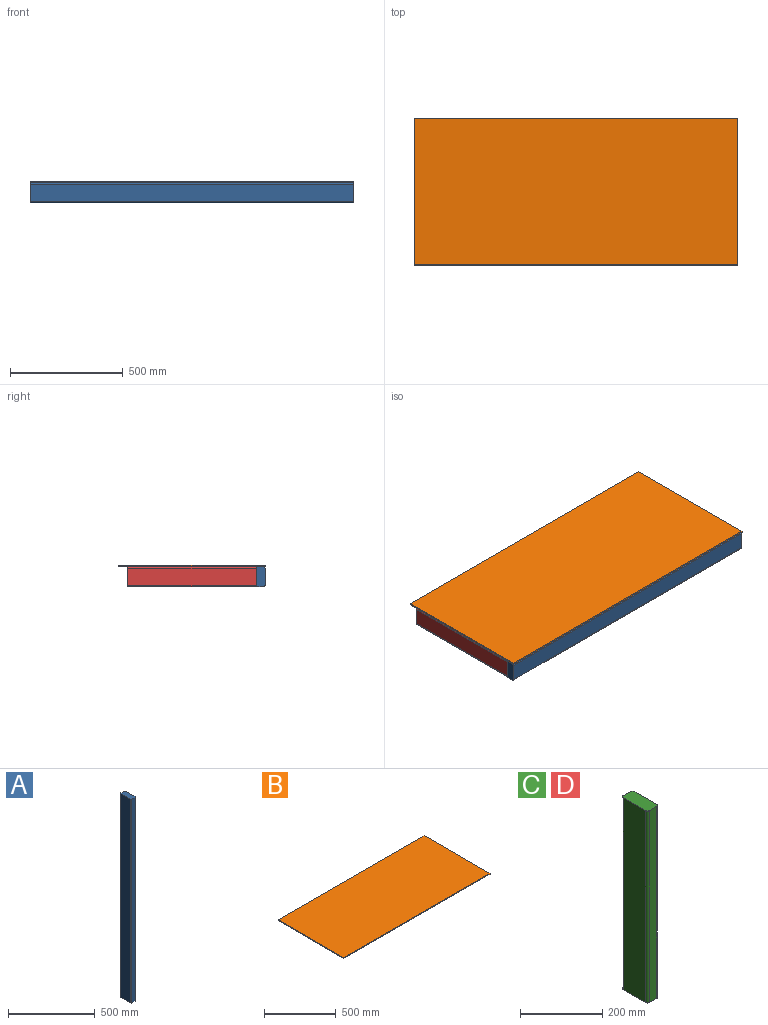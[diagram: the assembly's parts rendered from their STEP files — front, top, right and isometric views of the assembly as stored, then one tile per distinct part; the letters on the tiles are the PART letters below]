
ASSEMBLY  parts=4 mates=9
PART A: 10 faces, bbox 38.1x88.9x1435.1 mm
  f0: plane 1435.1x76.2mm, normal (-1,0,0), area 109354.6mm2, adj f1,f7,f8,f9
  f1: cylinder r=6.35mm len=1435.1mm, axis (0,0,-1), area 14314.5mm2, adj f0,f2,f8,f9
  f2: plane 1435.1x25.4mm, normal (0,-1,0), area 36451.5mm2, adj f1,f3,f8,f9
  f3: cylinder r=6.35mm len=1435.1mm, axis (0,0,-1), area 14314.5mm2, adj f2,f4,f8,f9
  f4: plane 1435.1x76.2mm, normal (1,0,0), area 109354.6mm2, adj f3,f5,f8,f9
  f5: cylinder r=6.35mm len=1435.1mm, axis (0,0,-1), area 14314.5mm2, adj f4,f6,f8,f9
  f6: plane 1435.1x25.4mm, normal (0,1,0), area 36451.5mm2, adj f5,f7,f8,f9
  f7: cylinder r=6.35mm len=1435.1mm, axis (0,0,-1), area 14314.5mm2, adj f0,f6,f8,f9
  f8: plane 88.9x38.1mm, normal (0,0,1), area 3352.5mm2, adj f0,f1,f2,f3,f4,f5,f6,f7
  f9: plane 88.9x38.1mm, normal (0,0,-1), area 3352.5mm2, adj f0,f1,f2,f3,f4,f5,f6,f7
PART B: 6 faces, bbox 1435.1x647.7x6.4 mm
  f0: plane 1435.1x6.35mm, normal (0,1,0), area 9112.9mm2, adj f1,f3,f4,f5
  f1: plane 647.7x6.35mm, normal (-1,0,0), area 4112.9mm2, adj f0,f2,f4,f5
  f2: plane 1435.1x6.35mm, normal (0,-1,0), area 9112.9mm2, adj f1,f3,f4,f5
  f3: plane 647.7x6.35mm, normal (1,0,0), area 4112.9mm2, adj f0,f2,f4,f5
  f4: plane 1435.1x647.7mm, normal (0,0,1), area 929514.3mm2, adj f0,f1,f2,f3
  f5: plane 1435.1x647.7mm, normal (0,0,-1), area 929514.3mm2, adj f0,f1,f2,f3
PART C: 10 faces, bbox 38.1x88.9x571.5 mm
  f0: plane 571.5x76.2mm, normal (-1,0,0), area 43548.3mm2, adj f1,f7,f8,f9
  f1: cylinder r=6.35mm len=571.5mm, axis (0,0,-1), area 5700.5mm2, adj f0,f2,f8,f9
  f2: plane 571.5x25.4mm, normal (0,-1,0), area 14516.1mm2, adj f1,f3,f8,f9
  f3: cylinder r=6.35mm len=571.5mm, axis (0,0,-1), area 5700.5mm2, adj f2,f4,f8,f9
  f4: plane 571.5x76.2mm, normal (1,0,0), area 43548.3mm2, adj f3,f5,f8,f9
  f5: cylinder r=6.35mm len=571.5mm, axis (0,0,-1), area 5700.5mm2, adj f4,f6,f8,f9
  f6: plane 571.5x25.4mm, normal (0,1,0), area 14516.1mm2, adj f5,f7,f8,f9
  f7: cylinder r=6.35mm len=571.5mm, axis (0,0,-1), area 5700.5mm2, adj f0,f6,f8,f9
  f8: plane 88.9x38.1mm, normal (0,0,1), area 3352.5mm2, adj f0,f1,f2,f3,f4,f5,f6,f7
  f9: plane 88.9x38.1mm, normal (0,0,-1), area 3352.5mm2, adj f0,f1,f2,f3,f4,f5,f6,f7
PART D: same geometry as C
PLACE A rot(axis=(-0.58,0.58,-0.58),120deg) t=(717.55,18.66,-50.15)mm
PLACE B t=(717.55,323.85,-6.35)mm
PLACE C rot(axis=(0,0.71,0.71),180deg) t=(1416.18,323.85,-50.67)mm
PLACE D rot(axis=(1,0,0),90deg) t=(18.92,323.85,-50.67)mm
MATE planar A.f4 <-> B.f2  axis (0,-1,0) through (717.55,0,-50.8)mm
MATE planar A.f8 <-> B.f3  axis (1,0,0) through (1435.1,19.05,-50.8)mm
MATE planar A.f2 <-> B.f5  axis (0,0,1) through (717.55,19.05,-6.35)mm
MATE planar B.f5 <-> D.f6  axis (0,0,-1) through (717.55,323.85,-6.35)mm
MATE planar C.f0 <-> B.f3  axis (1,0,0) through (1435.1,323.85,-50.8)mm
MATE planar C.f9 <-> A.f0  axis (0,-1,0) through (1416.05,38.1,-50.8)mm
MATE planar D.f0 <-> B.f1  axis (-1,0,0) through (0,323.85,-50.8)mm
MATE planar D.f8 <-> A.f0  axis (0,-1,0) through (19.05,38.1,-50.8)mm
MATE planar C.f6 <-> B.f5  axis (0,0,1) through (1416.05,323.85,-6.35)mm
